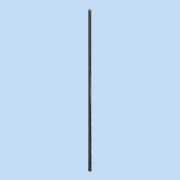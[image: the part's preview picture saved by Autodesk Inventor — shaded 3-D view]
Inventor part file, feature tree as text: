
AUTODESK INVENTOR PART (.ipt)
format: ipt  version: 2015 (Build 190159000, 159)  size: 82,944 bytes
history: native  units: mm
features: extrude x1, sketch x1
ambient origin geometry x8: Origin, YZ Plane, XZ Plane, XY Plane, X Axis, Y Axis, Z Axis, Center Point
bodies: Solid1 (feature_tree)
feature tree (2):
  extrude  "Extrusion1"  Depth=340.0mm TaperAngle=0.0deg
  sketch  "Sketch1"  dims[d0=6.0mm d1=340.0mm d2=0.0mm]
